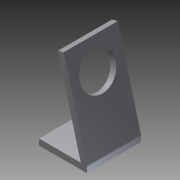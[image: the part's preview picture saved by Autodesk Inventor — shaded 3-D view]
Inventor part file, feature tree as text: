
AUTODESK INVENTOR PART (.ipt)
format: ipt  version: 2012 (Build 160160000, 160)  size: 93,696 bytes
history: native  units: in
note: dims shown in document units (in); Inventor stores cm internally (conversion verified against a paired STEP export)
features: extrude x2, sketch x2, fillet x1
ambient origin geometry x8: Origin, YZ Plane, XZ Plane, XY Plane, X Axis, Y Axis, Z Axis, Center Point
bodies: Solid1 (feature_tree)
feature tree (5):
  extrude  "Extrusion1"  Depth=1.0in
  extrude  "Extrusion2"  TaperAngle=75.0deg  [1 undecoded]
  fillet  "Fillet1"  Radius=1.875in
  sketch  "Sketch1"  dims[d0=0.125in d1=1.0in]
  sketch  "Sketch2"  dims[d3=0.125in d4=75.0deg d5=1.875in d6=1.125in d7=0.0in d8=0.75in d9=0.5625in d10=0.5625in d11=1.125in d12=0.0in d13=0.125in]
note: 1 required parameter value undecoded (feature->parameter linkage not recoverable at this tier; creation-order binding heuristic only, values carry confidence <= 0.55)
